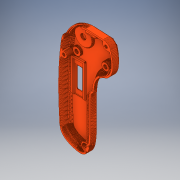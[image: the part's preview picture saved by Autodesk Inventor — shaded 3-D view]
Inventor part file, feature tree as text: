
AUTODESK INVENTOR PART (.ipt)
format: ipt  version: 2019.4 (Build 234330000, 330)  size: 9,394,176 bytes
history: native  units: mm
features: shell x1, other x1
ambient origin geometry x8: Origin, YZ Plane, XZ Plane, XY Plane, X Axis, Y Axis, Z Axis, Center Point
bodies: Solid1 (feature_tree)
feature tree (2):
  shell  "shell-top"  [1 undecoded]
  other  "MeshFeature1"
note: 1 required parameter value undecoded (feature->parameter linkage not recoverable at this tier; creation-order binding heuristic only, values carry confidence <= 0.55)
